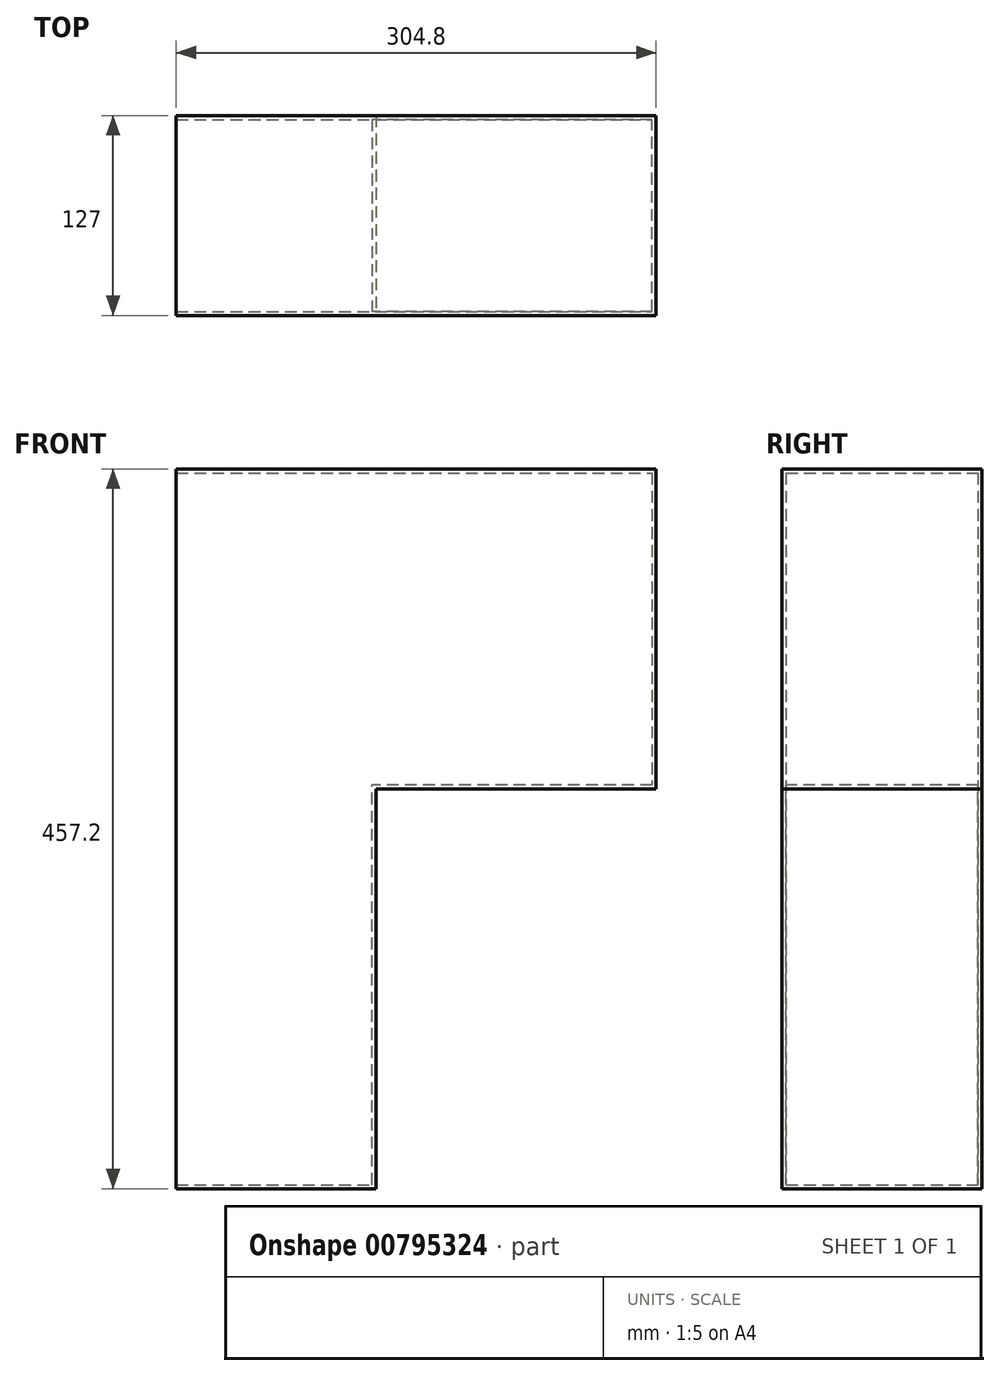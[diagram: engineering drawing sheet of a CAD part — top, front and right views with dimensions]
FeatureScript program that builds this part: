
annotation { "Feature Type Name" : "Feature", "Feature Type Description" : "" }
export const myFeature = defineFeature(function(context is Context, id is Id, definition is map)
    precondition{}
    {
        {
            var Q0;
            Q0=qCreatedBy(makeId("Front.planeOp"),FACE);
            var sketch = newSketch(context, id + "F0", { "sketchPlane" : qUnion([Q0])});
            skLineSegment(sketch, "E0.bottom", {"start": v(-195.73, 227.83) * mm, "end": v(109.07, 227.83) * mm});
            skLineSegment(sketch, "E0.top", {"start": v(-195.73, -229.37) * mm, "end": v(109.07, -229.37) * mm});
            skLineSegment(sketch, "E0.left", {"start": v(-195.73, 227.83) * mm, "end": v(-195.73, -229.37) * mm});
            skLineSegment(sketch, "E0.right", {"start": v(109.07, 227.83) * mm, "end": v(109.07, -229.37) * mm});
            skSolve(sketch);
        }
        {
            var Q0;
            Q0 = qSketchRegion(id + "F0", true);
            extrude(context, id + "F1", {"entities" : qUnion([Q0]), "depth" : 127 * mm, "offsetDistance" : 25.4 * mm});
        }
        {
            var Q0;
            Q0=makeQuery(id+"F1.opExtrude","CAP_FACE",FACE,{"disambiguationData":[OSD([sQuery(id+"F0.wireOp",EDGE,"E0.bottom"),sQuery(id+"F0.wireOp",EDGE,"E0.top"),sQuery(id+"F0.wireOp",EDGE,"E0.left"),sQuery(id+"F0.wireOp",EDGE,"E0.right")])],"isStart":false});
            var sketch = newSketch(context, id + "F2", { "sketchPlane" : qUnion([Q0])});
            skLineSegment(sketch, "E1.bottom", {"start": v(109.07, -229.37) * mm, "end": v(-68.73, -229.37) * mm});
            skLineSegment(sketch, "E1.top", {"start": v(109.07, 24.63) * mm, "end": v(-68.73, 24.63) * mm});
            skLineSegment(sketch, "E1.left", {"start": v(109.07, -229.37) * mm, "end": v(109.07, 24.63) * mm});
            skLineSegment(sketch, "E1.right", {"start": v(-68.73, -229.37) * mm, "end": v(-68.73, 24.63) * mm});
            skSolve(sketch);
        }
        {
            var Q0;
            Q0 = qSketchRegion(id + "F2", true);
            extrude(context, id + "F3", {"entities" : qUnion([Q0]), "operationType" : NewBodyOperationType.REMOVE, "oppositeDirection" : true, "depth" : 127 * mm, "offsetDistance" : 25.4 * mm});
        }
        {
            var Q0;
            Q0=makeQuery(id+"F1.opExtrude","SWEPT_FACE",FACE,{"disambiguationData":[OSD([sQuery(id+"F0.wireOp",EDGE,"E0.left")])]});
            shell(context, id + "F4", {"entities" : qUnion([Q0]), "thickness" : 2.54 * mm});
        }
    });
